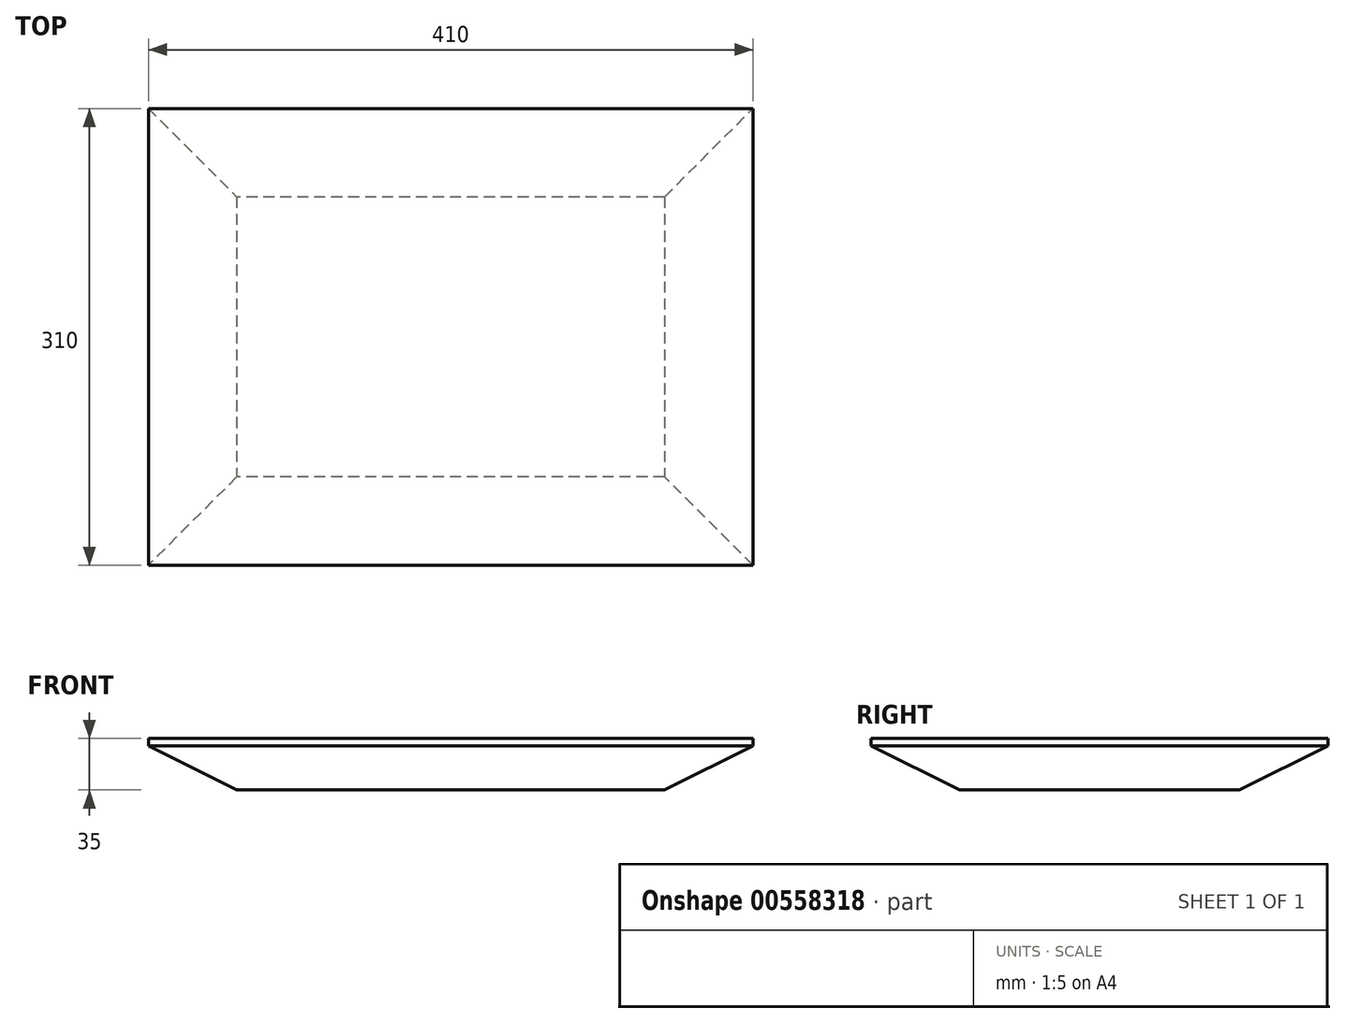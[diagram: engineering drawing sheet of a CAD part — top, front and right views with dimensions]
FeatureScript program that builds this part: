
annotation { "Feature Type Name" : "Feature", "Feature Type Description" : "" }
export const myFeature = defineFeature(function(context is Context, id is Id, definition is map)
    precondition{}
    {
        {
            var Q0;
            Q0=qCreatedBy(makeId("Top.planeOp"),FACE);
            var sketch = newSketch(context, id + "F0", { "sketchPlane" : qUnion([Q0])});
            skLineSegment(sketch, "E0.bottom", {"start": v(205, -155) * mm, "end": v(-205, -155) * mm});
            skLineSegment(sketch, "E0.top", {"start": v(205, 155) * mm, "end": v(-205, 155) * mm});
            skLineSegment(sketch, "E0.left", {"start": v(205, -155) * mm, "end": v(205, 155) * mm});
            skLineSegment(sketch, "E0.right", {"start": v(-205, -155) * mm, "end": v(-205, 155) * mm});
            skPoint(sketch, "E0.middle", {"position": v(0, 0) * mm});
            skSolve(sketch);
        }
        {
            var Q0;
            Q0 = qSketchRegion(id + "F0", true);
            extrude(context, id + "F1", {"entities" : qUnion([Q0]), "depth" : 35 * mm, "offsetDistance" : 25 * mm});
        }
        {
            var Q0;
            Q0=makeQuery(id+"F1.opExtrude","SWEPT_FACE",FACE,{"disambiguationData":[OSD([sQuery(id+"F0.wireOp",EDGE,"E0.bottom")])]});
            var sketch = newSketch(context, id + "F2", { "sketchPlane" : qUnion([Q0])});
            skLineSegment(sketch, "E1", {"start": v(-145, 0) * mm, "end": v(-205, 30) * mm});
            skLineSegment(sketch, "E2", {"start": v(-205, 30) * mm, "end": v(-247.47, 11.41) * mm});
            skLineSegment(sketch, "E3", {"start": v(-247.47, 11.41) * mm, "end": v(-186.29, -45.12) * mm});
            skLineSegment(sketch, "E4", {"start": v(-186.29, -45.12) * mm, "end": v(-145, 0) * mm});
            skSolve(sketch);
        }
        {
            var Q0;
            Q0 = qSketchRegion(id + "F2", true);
            extrude(context, id + "F3", {"entities" : qUnion([Q0]), "oppositeDirection" : true, "depth" : 413 * mm, "offsetDistance" : 25 * mm});
        }
        {
            var Q0;
            Q0=makeQuery(id+"F3.opExtrude","SWEPT_BODY",BODY,{"disambiguationData":[OSD([sQuery(id+"F2.wireOp",EDGE,"E1"),sQuery(id+"F2.wireOp",EDGE,"E2"),sQuery(id+"F2.wireOp",EDGE,"E3"),sQuery(id+"F2.wireOp",EDGE,"E4")])]});
            var Q1;
            Q1=qCreatedBy(makeId("Right.planeOp"),FACE);
            mirror(context, id + "F4", {"entities" : qUnion([Q0]), "mirrorPlane" : qUnion([Q1])});
        }
        {
            var Q0;
            Q0=makeQuery(id+"F3.opExtrude","SWEPT_BODY",BODY,{"disambiguationData":[OSD([sQuery(id+"F2.wireOp",EDGE,"E1"),sQuery(id+"F2.wireOp",EDGE,"E2"),sQuery(id+"F2.wireOp",EDGE,"E3"),sQuery(id+"F2.wireOp",EDGE,"E4")])]});
            var Q1;
            Q1=makeQuery(id+"F4.opPattern","COPY",BODY,{"derivedFrom":makeQuery(id+"F3.opExtrude","SWEPT_BODY",BODY,{"disambiguationData":[OSD([sQuery(id+"F2.wireOp",EDGE,"E1"),sQuery(id+"F2.wireOp",EDGE,"E2"),sQuery(id+"F2.wireOp",EDGE,"E3"),sQuery(id+"F2.wireOp",EDGE,"E4")])]}),"instanceName":"1"});
            var Q2;
            Q2=makeQuery(id+"F1.opExtrude","SWEPT_BODY",BODY,{"disambiguationData":[OSD([sQuery(id+"F0.wireOp",EDGE,"E0.bottom"),sQuery(id+"F0.wireOp",EDGE,"E0.top"),sQuery(id+"F0.wireOp",EDGE,"E0.left"),sQuery(id+"F0.wireOp",EDGE,"E0.right")])]});
            booleanBodies(context, id + "F5", {"operationType" : BooleanOperationType.SUBTRACTION, "tools" : qUnion([Q0, Q1]), "targets" : qUnion([Q2])});
        }
        {
            var Q0;
            Q0=makeQuery(id+"F1.opExtrude","SWEPT_FACE",FACE,{"disambiguationData":[OSD([sQuery(id+"F0.wireOp",EDGE,"E0.right")])]});
            var sketch = newSketch(context, id + "F6", { "sketchPlane" : qUnion([Q0])});
            skLineSegment(sketch, "E5", {"start": v(-95, 0) * mm, "end": v(-155, 30) * mm});
            skLineSegment(sketch, "E6", {"start": v(-155, 30) * mm, "end": v(-189.2, 15.52) * mm});
            skLineSegment(sketch, "E7", {"start": v(-189.2, 15.52) * mm, "end": v(-155, -27.47) * mm});
            skLineSegment(sketch, "E8", {"start": v(-155, -27.47) * mm, "end": v(-95, 0) * mm});
            skSolve(sketch);
        }
        {
            var Q0;
            Q0 = qSketchRegion(id + "F6", true);
            extrude(context, id + "F7", {"entities" : qUnion([Q0]), "oppositeDirection" : true, "depth" : 455 * mm, "offsetDistance" : 25 * mm});
        }
        {
            var Q0;
            Q0=makeQuery(id+"F7.opExtrude","SWEPT_BODY",BODY,{"disambiguationData":[OSD([sQuery(id+"F6.wireOp",EDGE,"E5"),sQuery(id+"F6.wireOp",EDGE,"E6"),sQuery(id+"F6.wireOp",EDGE,"E7"),sQuery(id+"F6.wireOp",EDGE,"E8")])]});
            var Q1;
            Q1=qCreatedBy(makeId("Front.planeOp"),FACE);
            mirror(context, id + "F8", {"entities" : qUnion([Q0]), "mirrorPlane" : qUnion([Q1])});
        }
        {
            var Q0;
            Q0=makeQuery(id+"F7.opExtrude","SWEPT_BODY",BODY,{"disambiguationData":[OSD([sQuery(id+"F6.wireOp",EDGE,"E5"),sQuery(id+"F6.wireOp",EDGE,"E6"),sQuery(id+"F6.wireOp",EDGE,"E7"),sQuery(id+"F6.wireOp",EDGE,"E8")])]});
            var Q1;
            Q1=makeQuery(id+"F8.opPattern","COPY",BODY,{"derivedFrom":makeQuery(id+"F7.opExtrude","SWEPT_BODY",BODY,{"disambiguationData":[OSD([sQuery(id+"F6.wireOp",EDGE,"E5"),sQuery(id+"F6.wireOp",EDGE,"E6"),sQuery(id+"F6.wireOp",EDGE,"E7"),sQuery(id+"F6.wireOp",EDGE,"E8")])]}),"instanceName":"1"});
            var Q2;
            Q2=makeQuery(id+"F1.opExtrude","SWEPT_BODY",BODY,{"disambiguationData":[OSD([sQuery(id+"F0.wireOp",EDGE,"E0.bottom"),sQuery(id+"F0.wireOp",EDGE,"E0.top"),sQuery(id+"F0.wireOp",EDGE,"E0.left"),sQuery(id+"F0.wireOp",EDGE,"E0.right")])]});
            booleanBodies(context, id + "F9", {"operationType" : BooleanOperationType.SUBTRACTION, "tools" : qUnion([Q0, Q1]), "targets" : qUnion([Q2])});
        }
    });
